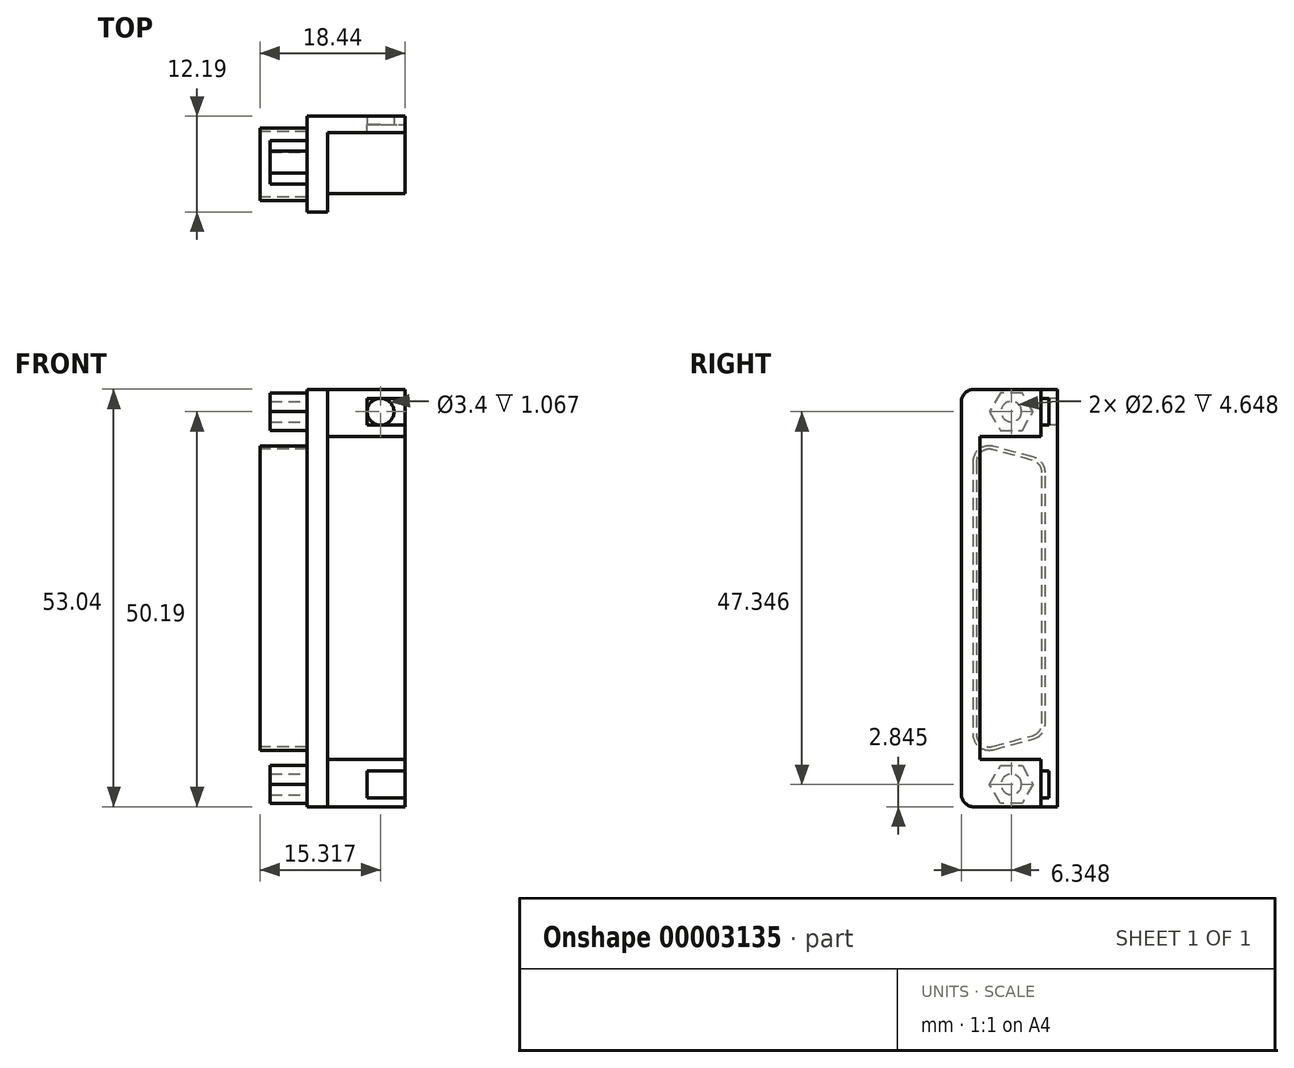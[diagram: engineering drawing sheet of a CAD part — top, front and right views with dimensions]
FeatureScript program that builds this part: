
annotation { "Feature Type Name" : "Feature", "Feature Type Description" : "" }
export const myFeature = defineFeature(function(context is Context, id is Id, definition is map)
    precondition{}
    {
        {
            var Q0;
            Q0=qCreatedBy(makeId("Right.planeOp"),FACE);
            var sketch = newSketch(context, id + "F0", { "sketchPlane" : qUnion([Q0])});
            skLineSegment(sketch, "E0.bottom", {"start": v(0, 0) * mm, "end": v(-10.6, 0) * mm});
            skLineSegment(sketch, "E0.top", {"start": v(0, 53.04) * mm, "end": v(-10.6, 53.04) * mm});
            skLineSegment(sketch, "E0.left", {"start": v(0, 0) * mm, "end": v(0, 53.04) * mm});
            skLineSegment(sketch, "E0.right", {"start": v(-12.2, 1.59) * mm, "end": v(-12.2, 51.45) * mm});
            skPoint(sketch, "E1.visualSharp", {"position": v(0, 53.04) * mm});
            skPoint(sketch, "E2.visualSharp", {"position": v(-12.2, 53.04) * mm});
            skArc(sketch, "E2.filletArc", {"start": v(-10.6, 53.04) * mm, "mid": v(-11.73, 52.57) * mm, "end": v(-12.2, 51.45) * mm});
            skPoint(sketch, "E3.visualSharp", {"position": v(-12.2, 0) * mm});
            skArc(sketch, "E3.filletArc", {"start": v(-12.2, 1.59) * mm, "mid": v(-11.73, 0.46) * mm, "end": v(-10.6, 0) * mm});
            skPoint(sketch, "E4.visualSharp", {"position": v(0, 0) * mm});
            skSolve(sketch);
        }
        {
            var Q0;
            Q0=makeQuery(id+"F0.imprint","IMPRINT",FACE,{"disambiguationData":[TD([[makeQuery(id+"F0.imprint","IMPRINT",EDGE,{"derivedFrom":sQuery(id+"F0.wireOp",EDGE,"E0.bottom")}),-1.0]])]});
            extrude(context, id + "F1", {"entities" : qUnion([Q0]), "depth" : 12.47 * mm});
        }
        {
            var Q0;
            Q0=makeQuery(id+"F1.opExtrude","CAP_FACE",FACE,{"disambiguationData":[OSD([sQuery(id+"F0.wireOp",EDGE,"E0.bottom"),sQuery(id+"F0.wireOp",EDGE,"E0.top"),sQuery(id+"F0.wireOp",EDGE,"E0.left"),sQuery(id+"F0.wireOp",EDGE,"E0.right"),sQuery(id+"F0.wireOp",EDGE,"E2.filletArc"),sQuery(id+"F0.wireOp",EDGE,"E3.filletArc")])],"isStart":false});
            var sketch = newSketch(context, id + "F2", { "sketchPlane" : qUnion([Q0])});
            skLineSegment(sketch, "E5", {"start": v(-2.08, 53.04) * mm, "end": v(-10.6, 53.04) * mm});
            skLineSegment(sketch, "E6", {"start": v(-12.2, 51.45) * mm, "end": v(-12.2, 1.59) * mm});
            skLineSegment(sketch, "E7", {"start": v(-10.6, 0) * mm, "end": v(-2.08, 0) * mm});
            skLineSegment(sketch, "E8", {"start": v(-2.08, 0) * mm, "end": v(-2.08, 6) * mm});
            skLineSegment(sketch, "E9", {"start": v(-2.08, 6) * mm, "end": v(-9.86, 6) * mm});
            skLineSegment(sketch, "E10", {"start": v(-9.86, 6) * mm, "end": v(-9.86, 47.04) * mm});
            skLineSegment(sketch, "E11", {"start": v(-9.86, 47.04) * mm, "end": v(-2.08, 47.04) * mm});
            skLineSegment(sketch, "E12", {"start": v(-2.08, 47.04) * mm, "end": v(-2.08, 53.04) * mm});
            skPoint(sketch, "E13.visualSharp", {"position": v(-12.2, 53.04) * mm});
            skArc(sketch, "E13.filletArc", {"start": v(-10.6, 53.04) * mm, "mid": v(-11.73, 52.57) * mm, "end": v(-12.2, 51.45) * mm});
            skPoint(sketch, "E14.visualSharp", {"position": v(-12.2, 0) * mm});
            skArc(sketch, "E14.filletArc", {"start": v(-12.2, 1.59) * mm, "mid": v(-11.73, 0.46) * mm, "end": v(-10.6, 0) * mm});
            skSolve(sketch);
        }
        {
            var Q0;
            Q0=makeQuery(id+"F2.imprint","IMPRINT",FACE,{"disambiguationData":[TD([[makeQuery(id+"F2.imprint","IMPRINT",EDGE,{"derivedFrom":sQuery(id+"F2.wireOp",EDGE,"E5")}),1.0]])]});
            extrude(context, id + "F3", {"entities" : qUnion([Q0]), "operationType" : NewBodyOperationType.REMOVE, "oppositeDirection" : true, "depth" : 9.88 * mm});
        }
        {
            var Q0;
            Q0=makeQuery(id+"F1.opExtrude","CAP_FACE",FACE,{"disambiguationData":[OSD([sQuery(id+"F0.wireOp",EDGE,"E0.bottom"),sQuery(id+"F0.wireOp",EDGE,"E0.top"),sQuery(id+"F0.wireOp",EDGE,"E0.left"),sQuery(id+"F0.wireOp",EDGE,"E0.right"),sQuery(id+"F0.wireOp",EDGE,"E2.filletArc"),sQuery(id+"F0.wireOp",EDGE,"E3.filletArc")])],"isStart":true});
            var sketch = newSketch(context, id + "F4", { "sketchPlane" : qUnion([Q0])});
            skLineSegment(sketch, "E15", {"start": v(10.72, 43.8) * mm, "end": v(10.72, 9.24) * mm});
            skLineSegment(sketch, "E16", {"start": v(8.12, 7.25) * mm, "end": v(3.05, 8.6) * mm});
            skLineSegment(sketch, "E17", {"start": v(1.52, 10.6) * mm, "end": v(1.52, 42.43) * mm});
            skLineSegment(sketch, "E18", {"start": v(3.05, 44.43) * mm, "end": v(8.12, 45.79) * mm});
            skPoint(sketch, "E19.visualSharp", {"position": v(10.72, 46.48) * mm});
            skArc(sketch, "E19.filletArc", {"start": v(10.72, 43.8) * mm, "mid": v(9.91, 45.43) * mm, "end": v(8.12, 45.79) * mm});
            skPoint(sketch, "E20.visualSharp", {"position": v(1.52, 44.02) * mm});
            skArc(sketch, "E20.filletArc", {"start": v(3.05, 44.43) * mm, "mid": v(1.95, 43.7) * mm, "end": v(1.52, 42.43) * mm});
            skPoint(sketch, "E21.visualSharp", {"position": v(1.52, 9.02) * mm});
            skArc(sketch, "E21.filletArc", {"start": v(1.52, 10.6) * mm, "mid": v(1.95, 9.34) * mm, "end": v(3.05, 8.6) * mm});
            skPoint(sketch, "E22.visualSharp", {"position": v(10.72, 6.55) * mm});
            skArc(sketch, "E22.filletArc", {"start": v(8.12, 7.25) * mm, "mid": v(9.91, 7.6) * mm, "end": v(10.72, 9.24) * mm});
            skSolve(sketch);
        }
        {
            var Q0;
            Q0=makeQuery(id+"F4.imprint","IMPRINT",FACE,{"disambiguationData":[TD([[makeQuery(id+"F4.imprint","IMPRINT",EDGE,{"derivedFrom":sQuery(id+"F4.wireOp",EDGE,"E15")}),-1.0]])]});
            extrude(context, id + "F5", {"entities" : qUnion([Q0]), "operationType" : NewBodyOperationType.ADD, "depth" : 5.97 * mm});
        }
        {
            var Q0;
            Q0=makeQuery(id+"F1.opExtrude","CAP_FACE",FACE,{"disambiguationData":[OSD([sQuery(id+"F0.wireOp",EDGE,"E0.bottom"),sQuery(id+"F0.wireOp",EDGE,"E0.top"),sQuery(id+"F0.wireOp",EDGE,"E0.left"),sQuery(id+"F0.wireOp",EDGE,"E0.right"),sQuery(id+"F0.wireOp",EDGE,"E2.filletArc"),sQuery(id+"F0.wireOp",EDGE,"E3.filletArc")])],"isStart":true});
            var sketch = newSketch(context, id + "F6", { "sketchPlane" : qUnion([Q0])});
            skCircle(sketch, "E23.cCircle", {"center": v(5.84, 50.2) * mm, "radius": 2.39 * mm, "construction": true});
            skLineSegment(sketch, "E23.0", {"start": v(8.6, 50.2) * mm, "end": v(7.22, 47.8) * mm});
            skLineSegment(sketch, "E23.1", {"start": v(7.22, 47.8) * mm, "end": v(4.46, 47.8) * mm});
            skLineSegment(sketch, "E23.2", {"start": v(4.46, 47.8) * mm, "end": v(3.09, 50.2) * mm});
            skLineSegment(sketch, "E23.3", {"start": v(3.09, 50.2) * mm, "end": v(4.46, 52.58) * mm});
            skLineSegment(sketch, "E23.4", {"start": v(4.46, 52.58) * mm, "end": v(7.22, 52.58) * mm});
            skLineSegment(sketch, "E23.5", {"start": v(7.22, 52.58) * mm, "end": v(8.6, 50.2) * mm});
            skPoint(sketch, "E23.0.midPoint", {"position": v(7.9, 49) * mm});
            skLineSegment(sketch, "E24", {"start": v(0, 26.52) * mm, "end": v(15.57, 26.52) * mm, "construction": true});
            skCircle(sketch, "E25", {"center": v(5.84, 50.2) * mm, "radius": 1.3 * mm});
            skLineSegment(sketch, "E26.0.MirrorCS", {"start": v(8.6, 2.84) * mm, "end": v(7.22, 5.23) * mm});
            skPoint(sketch, "E26.1.MirrorP", {"position": v(7.9, 4.04) * mm});
            skCircle(sketch, "E26.2.MirrorC", {"center": v(5.84, 2.84) * mm, "radius": 2.39 * mm, "construction": true});
            skCircle(sketch, "E26.3.MirrorC", {"center": v(5.84, 2.84) * mm, "radius": 1.3 * mm});
            skLineSegment(sketch, "E26.4.MirrorCS", {"start": v(4.46, 0.46) * mm, "end": v(7.22, 0.46) * mm});
            skLineSegment(sketch, "E26.5.MirrorCS", {"start": v(3.09, 2.84) * mm, "end": v(4.46, 0.46) * mm});
            skLineSegment(sketch, "E26.6.MirrorCS", {"start": v(4.46, 5.23) * mm, "end": v(3.09, 2.84) * mm});
            skLineSegment(sketch, "E26.7.MirrorCS", {"start": v(7.22, 5.23) * mm, "end": v(4.46, 5.23) * mm});
            skLineSegment(sketch, "E26.8.MirrorCS", {"start": v(7.22, 0.46) * mm, "end": v(8.6, 2.84) * mm});
            skSolve(sketch);
        }
        {
            var Q0;
            {Q0=qUnion([makeQuery(id+"F6.imprint","IMPRINT",FACE,{"disambiguationData":[TD([[makeQuery(id+"F6.imprint","IMPRINT",EDGE,{"derivedFrom":sQuery(id+"F6.wireOp",EDGE,"E23.0")}),-1.0]])]}),makeQuery(id+"F6.imprint","IMPRINT",FACE,{"disambiguationData":[TD([[makeQuery(id+"F6.imprint","IMPRINT",EDGE,{"derivedFrom":sQuery(id+"F6.wireOp",EDGE,"E26.0.MirrorCS")}),1.0]])]})]);}
            extrude(context, id + "F7", {"entities" : qUnion([Q0]), "operationType" : NewBodyOperationType.ADD, "depth" : 4.65 * mm});
        }
        {
            var Q0;
            Q0=makeQuery(id+"F3.boolean.opBoolean","COPY",FACE,{"derivedFrom":makeQuery(id+"F3.opExtrude","SWEPT_FACE",FACE,{"disambiguationData":[OSD([sQuery(id+"F2.wireOp",EDGE,"E12")])]})});
            var sketch = newSketch(context, id + "F8", { "sketchPlane" : qUnion([Q0])});
            skCircle(sketch, "E27", {"center": v(9.35, 50.2) * mm, "radius": 1.7 * mm});
            skLineSegment(sketch, "E28", {"start": v(7.53, 0) * mm, "end": v(7.53, 53.04) * mm, "construction": true});
            skLineSegment(sketch, "E29", {"start": v(7.53, 26.52) * mm, "end": v(15.08, 26.52) * mm, "construction": true});
            skCircle(sketch, "E30.0.MirrorC", {"center": v(9.35, 2.84) * mm, "radius": 1.7 * mm});
            skSolve(sketch);
        }
        {
            var Q0;
            {Q0=qUnion([makeQuery(id+"F8.imprint","IMPRINT",FACE,{"disambiguationData":[TD([[makeQuery(id+"F8.imprint","IMPRINT",EDGE,{"derivedFrom":sQuery(id+"F8.wireOp",EDGE,"E30.0.MirrorC")}),-1.0]])]}),makeQuery(id+"F8.imprint","IMPRINT",FACE,{"disambiguationData":[TD([[makeQuery(id+"F8.imprint","IMPRINT",EDGE,{"derivedFrom":sQuery(id+"F8.wireOp",EDGE,"E27")}),1.0]])]})]);}
            extrude(context, id + "F9", {"entities" : qUnion([Q0]), "operationType" : NewBodyOperationType.REMOVE, "endBound" : BoundingType.UP_TO_NEXT, "oppositeDirection" : true, "depth" : 25.4 * mm});
        }
        {
            var Q0;
            Q0=makeQuery(id+"F5.opExtrude","CAP_FACE",FACE,{"disambiguationData":[OSD([sQuery(id+"F4.wireOp",EDGE,"E15"),sQuery(id+"F4.wireOp",EDGE,"E16"),sQuery(id+"F4.wireOp",EDGE,"E17"),sQuery(id+"F4.wireOp",EDGE,"E18"),sQuery(id+"F4.wireOp",EDGE,"E19.filletArc"),sQuery(id+"F4.wireOp",EDGE,"E20.filletArc"),sQuery(id+"F4.wireOp",EDGE,"E21.filletArc"),sQuery(id+"F4.wireOp",EDGE,"E22.filletArc")])],"isStart":false});
            var sketch = newSketch(context, id + "F10", { "sketchPlane" : qUnion([Q0])});
            skLineSegment(sketch, "E31.0", {"start": v(3.17, 44.01) * mm, "end": v(8.23, 45.37) * mm});
            skArc(sketch, "E31.1", {"start": v(10.29, 43.8) * mm, "mid": v(9.65, 45.09) * mm, "end": v(8.23, 45.37) * mm});
            skLineSegment(sketch, "E31.2", {"start": v(10.29, 43.8) * mm, "end": v(10.29, 9.24) * mm});
            skArc(sketch, "E31.3", {"start": v(8.23, 7.67) * mm, "mid": v(9.65, 7.95) * mm, "end": v(10.29, 9.24) * mm});
            skLineSegment(sketch, "E31.4", {"start": v(8.23, 7.67) * mm, "end": v(3.17, 9.02) * mm});
            skArc(sketch, "E31.5", {"start": v(3.17, 44.01) * mm, "mid": v(2.3, 43.43) * mm, "end": v(1.96, 42.43) * mm});
            skArc(sketch, "E31.6", {"start": v(1.96, 10.6) * mm, "mid": v(2.3, 9.6) * mm, "end": v(3.17, 9.02) * mm});
            skLineSegment(sketch, "E31.7", {"start": v(1.96, 10.6) * mm, "end": v(1.96, 42.43) * mm});
            skSolve(sketch);
        }
        {
            var Q0;
            Q0=makeQuery(id+"F10.imprint","IMPRINT",FACE,{"disambiguationData":[TD([[makeQuery(id+"F10.imprint","IMPRINT",EDGE,{"derivedFrom":sQuery(id+"F10.wireOp",EDGE,"E31.0")}),-1.0]])]});
            var Q1;
            {var subQ0=sQuery(id+"F0.wireOp",EDGE,"E0.bottom");var subQ1=sQuery(id+"F0.wireOp",EDGE,"E0.top");var subQ2=sQuery(id+"F0.wireOp",EDGE,"E0.left");var subQ3=sQuery(id+"F0.wireOp",EDGE,"E0.right");var subQ4=sQuery(id+"F0.wireOp",EDGE,"E2.filletArc");var subQ5=sQuery(id+"F0.wireOp",EDGE,"E3.filletArc");Q1=makeQuery(id+"F7.boolean.opBoolean","SPLIT",FACE,{"disambiguationData":[TD([makeQuery(id+"F1.opExtrude","SWEPT_FACE",FACE,{"disambiguationData":[OSD([subQ0])]})])],"derivedFrom":makeQuery(id+"F1.opExtrude","CAP_FACE",FACE,{"disambiguationData":[OSD([subQ0,subQ1,subQ2,subQ3,subQ4,subQ5])],"isStart":true})});}
            extrude(context, id + "F11", {"entities" : qUnion([Q0]), "operationType" : NewBodyOperationType.REMOVE, "endBound" : BoundingType.UP_TO_SURFACE, "oppositeDirection" : true, "endBoundEntityFace" : qUnion([Q1]), "depth" : 25.4 * mm});
        }
        {
            var Q0;
            Q0=makeQuery(id+"F1.opExtrude","CAP_FACE",FACE,{"disambiguationData":[OSD([sQuery(id+"F0.wireOp",EDGE,"E0.bottom"),sQuery(id+"F0.wireOp",EDGE,"E0.top"),sQuery(id+"F0.wireOp",EDGE,"E0.left"),sQuery(id+"F0.wireOp",EDGE,"E0.right"),sQuery(id+"F0.wireOp",EDGE,"E2.filletArc"),sQuery(id+"F0.wireOp",EDGE,"E3.filletArc")])],"isStart":false});
            var sketch = newSketch(context, id + "F12", { "sketchPlane" : qUnion([Q0])});
            skLineSegment(sketch, "E32.bottom", {"start": v(-2.08, 48.49) * mm, "end": v(-1.07, 48.49) * mm});
            skLineSegment(sketch, "E32.top", {"start": v(-2.08, 51.9) * mm, "end": v(-1.07, 51.9) * mm});
            skLineSegment(sketch, "E32.left", {"start": v(-2.08, 48.49) * mm, "end": v(-2.08, 51.9) * mm});
            skLineSegment(sketch, "E32.right", {"start": v(-1.07, 48.49) * mm, "end": v(-1.07, 51.9) * mm});
            skLineSegment(sketch, "E33", {"start": v(0, 26.52) * mm, "end": v(-14.84, 26.52) * mm, "construction": true});
            skLineSegment(sketch, "E34", {"start": v(-2.08, 50.2) * mm, "end": v(1.44, 50.2) * mm, "construction": true});
            skLineSegment(sketch, "E35.0.MirrorCS", {"start": v(-2.08, 4.55) * mm, "end": v(-1.07, 4.55) * mm});
            skLineSegment(sketch, "E35.1.MirrorCS", {"start": v(-2.08, 1.14) * mm, "end": v(-1.07, 1.14) * mm});
            skLineSegment(sketch, "E35.2.MirrorCS", {"start": v(-1.07, 4.55) * mm, "end": v(-1.07, 1.14) * mm});
            skLineSegment(sketch, "E35.3.MirrorCS", {"start": v(-2.08, 4.55) * mm, "end": v(-2.08, 1.14) * mm});
            skSolve(sketch);
        }
        {
            var Q0;
            {Q0=qUnion([makeQuery(id+"F12.imprint","IMPRINT",FACE,{"disambiguationData":[TD([[makeQuery(id+"F12.imprint","IMPRINT",EDGE,{"derivedFrom":sQuery(id+"F12.wireOp",EDGE,"E32.bottom")}),1.0]])]}),makeQuery(id+"F12.imprint","IMPRINT",FACE,{"disambiguationData":[TD([[makeQuery(id+"F12.imprint","IMPRINT",EDGE,{"derivedFrom":sQuery(id+"F12.wireOp",EDGE,"E35.0.MirrorCS")}),-1.0]])]})]);}
            extrude(context, id + "F13", {"entities" : qUnion([Q0]), "operationType" : NewBodyOperationType.REMOVE, "oppositeDirection" : true, "depth" : 4.83 * mm});
        }
    });
